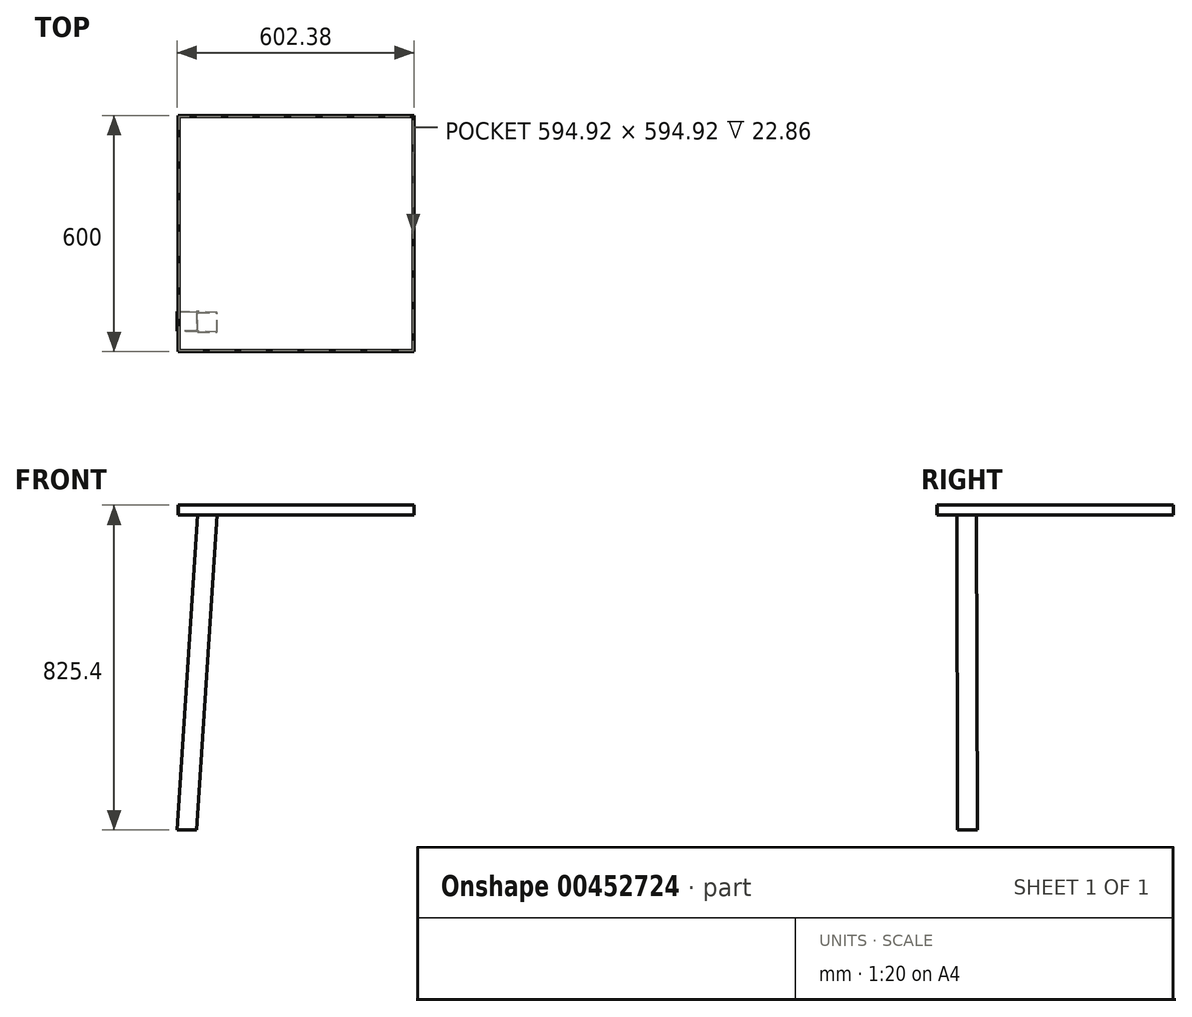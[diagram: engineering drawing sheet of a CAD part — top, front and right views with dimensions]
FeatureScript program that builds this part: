
annotation { "Feature Type Name" : "Feature", "Feature Type Description" : "" }
export const myFeature = defineFeature(function(context is Context, id is Id, definition is map)
    precondition{}
    {
        {
            var Q0;
            Q0=qCreatedBy(makeId("Front.planeOp"),FACE);
            var sketch = newSketch(context, id + "F0", { "sketchPlane" : qUnion([Q0])});
            skLineSegment(sketch, "E0.bottom", {"start": v(-300, 25.4) * mm, "end": v(300, 25.4) * mm});
            skLineSegment(sketch, "E0.top", {"start": v(-300, 0) * mm, "end": v(300, 0) * mm});
            skLineSegment(sketch, "E0.left", {"start": v(-300, 25.4) * mm, "end": v(-300, 0) * mm});
            skLineSegment(sketch, "E0.right", {"start": v(300, 25.4) * mm, "end": v(300, 0) * mm});
            skLineSegment(sketch, "E1", {"start": v(-250, 0) * mm, "end": v(250, 0) * mm});
            skSolve(sketch);
        }
        {
            var Q0;
            Q0 = qSketchRegion(id + "F0", true);
            extrude(context, id + "F1", {"entities" : qUnion([Q0]), "depth" : 600 * mm});
        }
        {
            var Q0;
            Q0=makeQuery(id+"F1.opExtrude","SWEPT_FACE",FACE,{"disambiguationData":[OSD([sQuery(id+"F0.wireOp",EDGE,"E0.bottom")])]});
            shell(context, id + "F2", {"entities" : qUnion([Q0]), "thickness" : 2.54 * mm});
        }
        {
            var Q0;
            Q0=makeQuery(id+"F1.opExtrude","SWEPT_FACE",FACE,{"disambiguationData":[OSD([sQuery(id+"F0.wireOp",EDGE,"E0.top"),sQuery(id+"F0.wireOp",EDGE,"E1")])]});
            var sketch = newSketch(context, id + "F3", { "sketchPlane" : qUnion([Q0])});
            skLineSegment(sketch, "E2.bottom", {"start": v(-250, 550) * mm, "end": v(-200, 550) * mm});
            skLineSegment(sketch, "E2.left", {"start": v(-250, 550) * mm, "end": v(-250, 500) * mm});
            skPoint(sketch, "E3.end.orphan", {"position": v(0, 50) * mm});
            skLineSegment(sketch, "E4.top", {"start": v(-250, 500) * mm, "end": v(-200, 500) * mm});
            skLineSegment(sketch, "E4.right", {"start": v(-200, 550) * mm, "end": v(-200, 500) * mm});
            skPoint(sketch, "E2.right.start.orphan", {"position": v(250, 550) * mm});
            skPoint(sketch, "E5.orphan", {"position": v(250, 50) * mm});
            skSolve(sketch);
        }
        {
            var Q0;
            Q0=qCreatedBy(makeId("Top.planeOp"),FACE);
            cPlane(context, id + "F4", {"entities" : qUnion([Q0]), "cplaneType" : CPlaneType.OFFSET, "offset" : 800 * mm, "oppositeDirection" : true, "width" : 152.4 * mm, "height" : 152.4 * mm});
        }
        {
            var Q0;
            Q0=qCreatedBy(id+"F4.planeOp",FACE);
            var sketch = newSketch(context, id + "F5", { "sketchPlane" : qUnion([Q0])});
            skLineSegment(sketch, "E6", {"start": v(-252.38, -548.17) * mm, "end": v(-302.38, -548.17) * mm});
            skLineSegment(sketch, "E7", {"start": v(-302.38, -548.17) * mm, "end": v(-302.38, -498.17) * mm});
            skLineSegment(sketch, "E8", {"start": v(-302.38, -498.17) * mm, "end": v(-252.38, -498.17) * mm});
            skLineSegment(sketch, "E9", {"start": v(-252.38, -498.17) * mm, "end": v(-252.38, -548.17) * mm});
            skLineSegment(sketch, "E10.MirrorCS", {"start": v(252.38, -498.17) * mm, "end": v(252.38, -548.17) * mm});
            skLineSegment(sketch, "E11.MirrorCS", {"start": v(252.38, -548.17) * mm, "end": v(302.38, -548.17) * mm});
            skLineSegment(sketch, "E12.MirrorCS", {"start": v(302.38, -548.17) * mm, "end": v(302.38, -498.17) * mm});
            skLineSegment(sketch, "E13.MirrorCS", {"start": v(302.38, -498.17) * mm, "end": v(252.38, -498.17) * mm});
            skLineSegment(sketch, "E14.MirrorCS", {"start": v(252.38, -102.3) * mm, "end": v(252.38, -52.3) * mm});
            skLineSegment(sketch, "E15.MirrorCS", {"start": v(252.38, -52.3) * mm, "end": v(302.38, -52.3) * mm});
            skLineSegment(sketch, "E16.MirrorCS", {"start": v(302.38, -52.3) * mm, "end": v(302.38, -102.3) * mm});
            skLineSegment(sketch, "E17.MirrorCS", {"start": v(302.38, -102.3) * mm, "end": v(252.38, -102.3) * mm});
            skLineSegment(sketch, "E18.MirrorCS", {"start": v(-252.38, -102.3) * mm, "end": v(-252.38, -52.3) * mm});
            skLineSegment(sketch, "E19.MirrorCS", {"start": v(-252.38, -52.3) * mm, "end": v(-302.38, -52.3) * mm});
            skLineSegment(sketch, "E20.MirrorCS", {"start": v(-302.38, -102.3) * mm, "end": v(-252.38, -102.3) * mm});
            skLineSegment(sketch, "E21", {"start": v(-302.38, -102.3) * mm, "end": v(-302.38, -52.3) * mm});
            skSolve(sketch);
        }
        {
            var Q1;
            Q1=makeQuery(id+"F3.imprint","IMPRINT",FACE,{"disambiguationData":[TD([[makeQuery(id+"F3.imprint","IMPRINT",EDGE,{"derivedFrom":sQuery(id+"F3.wireOp",EDGE,"E2.bottom")}),-1.0]])]});
            var Q2;
            Q2=makeQuery(id+"F5.imprint","IMPRINT",FACE,{"disambiguationData":[TD([[makeQuery(id+"F5.imprint","IMPRINT",EDGE,{"derivedFrom":sQuery(id+"F5.wireOp",EDGE,"E6")}),-1.0]])]});
            loft(context, id + "F6", {"operationType" : NewBodyOperationType.ADD, "sheetProfilesArray" : [{ "sheetProfileEntities" : qUnion([Q1]) }, { "sheetProfileEntities" : qUnion([Q2]) }]});
        }
    });
